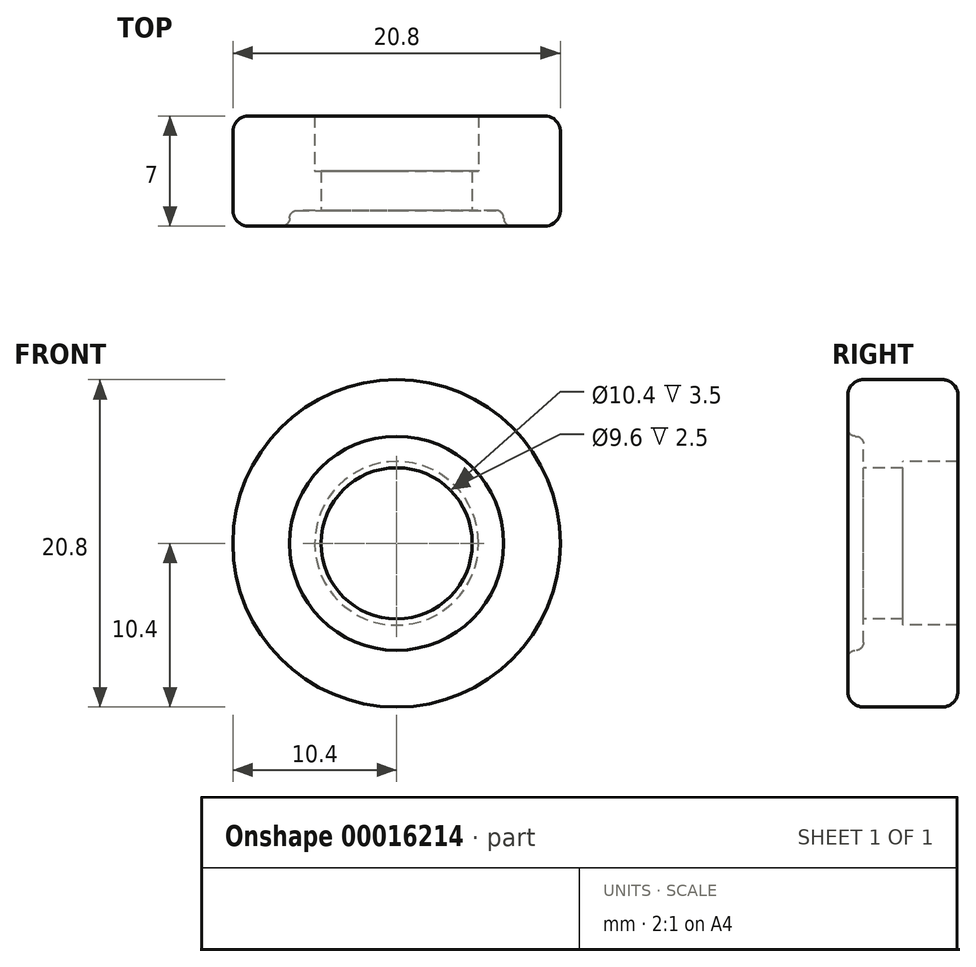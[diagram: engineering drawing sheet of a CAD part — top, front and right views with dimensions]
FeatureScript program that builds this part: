
annotation { "Feature Type Name" : "Feature", "Feature Type Description" : "" }
export const myFeature = defineFeature(function(context is Context, id is Id, definition is map)
    precondition{}
    {
        {
            var Q0;
            Q0=qCreatedBy(makeId("Top.planeOp"),FACE);
            var sketch = newSketch(context, id + "F0", { "sketchPlane" : qUnion([Q0])});
            skLineSegment(sketch, "E0", {"start": v(0, 0) * mm, "end": v(0, 6.54) * mm, "construction": true});
            skLineSegment(sketch, "E1", {"start": v(5.2, 0) * mm, "end": v(5.2, -3.5) * mm});
            skLineSegment(sketch, "E2", {"start": v(4.8, -3.5) * mm, "end": v(5.2, -3.5) * mm});
            skLineSegment(sketch, "E3", {"start": v(4.8, -3.5) * mm, "end": v(4.8, -6) * mm});
            skLineSegment(sketch, "E4", {"start": v(7.3, -7) * mm, "end": v(9.4, -7) * mm});
            skLineSegment(sketch, "E5", {"start": v(5.2, 0) * mm, "end": v(9.4, 0) * mm});
            skLineSegment(sketch, "E6", {"start": v(10.4, -1) * mm, "end": v(10.4, -6) * mm});
            skPoint(sketch, "E7.visualSharp", {"position": v(10.4, 0) * mm});
            skArc(sketch, "E7.filletArc", {"start": v(10.4, -1) * mm, "mid": v(10.1, -0.3) * mm, "end": v(9.4, 0) * mm});
            skPoint(sketch, "E8.visualSharp", {"position": v(10.4, -7) * mm});
            skArc(sketch, "E8.filletArc", {"start": v(9.4, -7) * mm, "mid": v(10.1, -6.7) * mm, "end": v(10.4, -6) * mm});
            skLineSegment(sketch, "E9", {"start": v(4.8, -6) * mm, "end": v(6.3, -6) * mm});
            skLineSegment(sketch, "E10", {"start": v(6.8, -6.5) * mm, "end": v(6.8, -6.5) * mm});
            skPoint(sketch, "E11.visualSharp", {"position": v(6.8, -7) * mm});
            skArc(sketch, "E11.filletArc", {"start": v(6.8, -6.5) * mm, "mid": v(6.95, -6.85) * mm, "end": v(7.3, -7) * mm});
            skPoint(sketch, "E12.visualSharp", {"position": v(6.8, -6) * mm});
            skArc(sketch, "E12.filletArc", {"start": v(6.8, -6.5) * mm, "mid": v(6.65, -6.15) * mm, "end": v(6.3, -6) * mm});
            skSolve(sketch);
        }
        {
            var Q0;
            Q0 = qSketchRegion(id + "F0", true);
            var Q1;
            Q1=sQuery(id+"F0.wireOp",EDGE,"E0");
            revolve(context, id + "F1", {"entities" : qUnion([Q0]), "axis" : qUnion([Q1]), "revolveType" : RevolveType.FULL});
        }
    });
